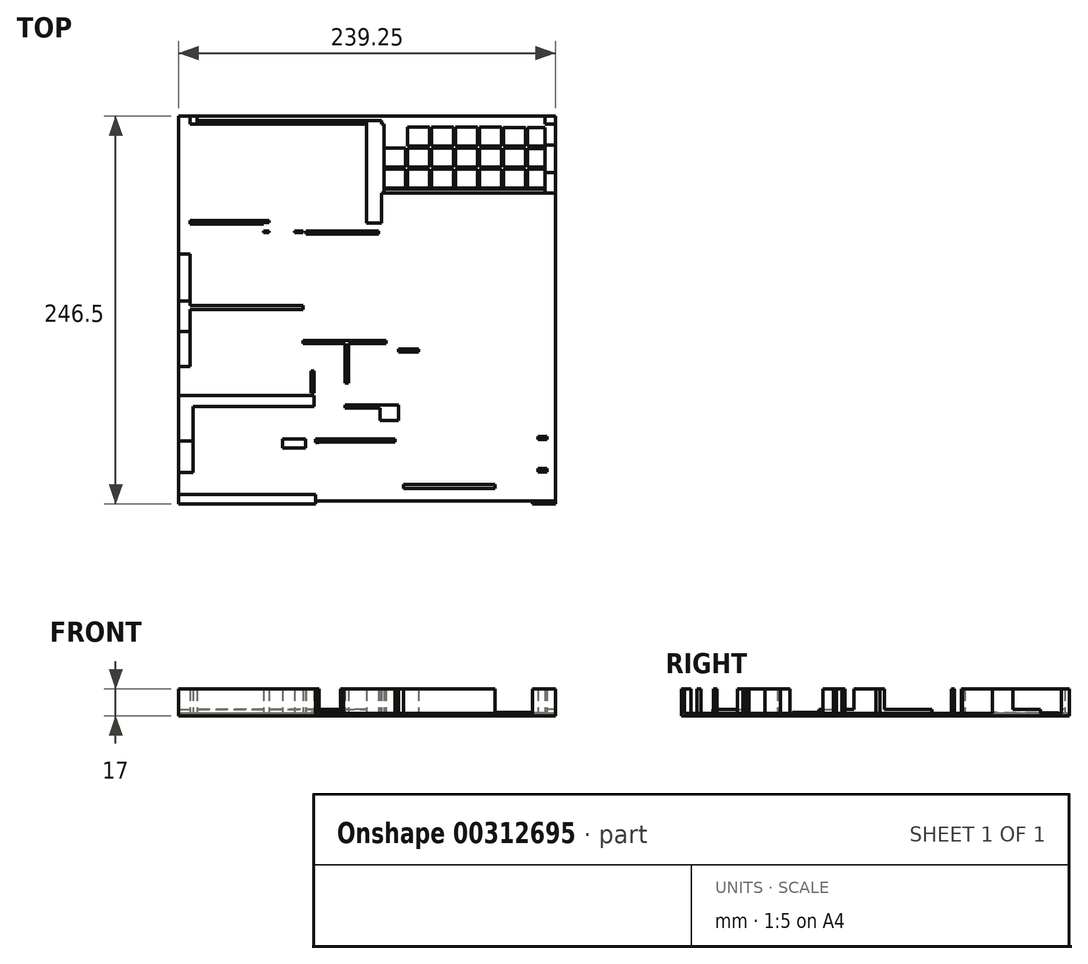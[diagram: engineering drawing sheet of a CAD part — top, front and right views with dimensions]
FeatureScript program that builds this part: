
annotation { "Feature Type Name" : "Feature", "Feature Type Description" : "" }
export const myFeature = defineFeature(function(context is Context, id is Id, definition is map)
    precondition{}
    {
        {
            var Q0;
            Q0=qCreatedBy(makeId("Top.planeOp"),FACE);
            var sketch = newSketch(context, id + "F0", { "sketchPlane" : qUnion([Q0])});
            skLineSegment(sketch, "E0.bottom", {"start": v(-71.69, -52.86) * mm, "end": v(15.31, -52.86) * mm});
            skLineSegment(sketch, "E0.top", {"start": v(-71.69, -46.86) * mm, "end": v(15.31, -46.86) * mm});
            skLineSegment(sketch, "E0.left", {"start": v(-71.69, -52.86) * mm, "end": v(-71.69, -46.86) * mm});
            skLineSegment(sketch, "E0.right", {"start": v(15.31, -52.86) * mm, "end": v(15.31, -46.86) * mm});
            skLineSegment(sketch, "E1.bottom", {"start": v(-71.69, -46.86) * mm, "end": v(-62.69, -46.86) * mm});
            skLineSegment(sketch, "E1.top", {"start": v(-71.69, -32.86) * mm, "end": v(-62.69, -32.86) * mm});
            skLineSegment(sketch, "E1.left", {"start": v(-71.69, -46.86) * mm, "end": v(-71.69, -32.86) * mm});
            skLineSegment(sketch, "E1.right", {"start": v(-62.69, -46.86) * mm, "end": v(-62.69, -32.86) * mm});
            skLineSegment(sketch, "E2.top", {"start": v(-71.69, -12.86) * mm, "end": v(-62.69, -12.86) * mm});
            skLineSegment(sketch, "E2.left", {"start": v(-71.69, -32.86) * mm, "end": v(-71.69, -12.86) * mm});
            skLineSegment(sketch, "E2.right", {"start": v(-62.69, -32.86) * mm, "end": v(-62.69, -12.86) * mm});
            skLineSegment(sketch, "E3.top", {"start": v(-71.69, 16.14) * mm, "end": v(-62.69, 16.14) * mm});
            skLineSegment(sketch, "E3.left", {"start": v(-71.69, -12.86) * mm, "end": v(-71.69, 16.14) * mm});
            skLineSegment(sketch, "E3.right", {"start": v(-62.69, -12.86) * mm, "end": v(-62.69, 16.14) * mm});
            skLineSegment(sketch, "E4.bottom", {"start": v(-71.69, 16.14) * mm, "end": v(-64.44, 16.14) * mm});
            skLineSegment(sketch, "E4.top", {"start": v(-71.69, 34.64) * mm, "end": v(-64.44, 34.64) * mm});
            skLineSegment(sketch, "E4.left", {"start": v(-71.69, 16.14) * mm, "end": v(-71.69, 34.64) * mm});
            skLineSegment(sketch, "E4.right", {"start": v(-64.44, 16.14) * mm, "end": v(-64.44, 34.64) * mm});
            skLineSegment(sketch, "E5.top", {"start": v(-71.69, 56.64) * mm, "end": v(-64.44, 56.64) * mm});
            skLineSegment(sketch, "E5.left", {"start": v(-71.69, 34.64) * mm, "end": v(-71.69, 56.64) * mm});
            skLineSegment(sketch, "E5.right", {"start": v(-64.44, 34.64) * mm, "end": v(-64.44, 56.64) * mm});
            skLineSegment(sketch, "E6.top", {"start": v(-71.69, 76.14) * mm, "end": v(-64.44, 76.14) * mm});
            skLineSegment(sketch, "E6.left", {"start": v(-71.69, 56.64) * mm, "end": v(-71.69, 76.14) * mm});
            skLineSegment(sketch, "E6.right", {"start": v(-64.44, 56.64) * mm, "end": v(-64.44, 76.14) * mm});
            skLineSegment(sketch, "E7.bottom", {"start": v(-62.69, 16.14) * mm, "end": v(14.31, 16.14) * mm});
            skLineSegment(sketch, "E7.top", {"start": v(-62.69, 9.14) * mm, "end": v(14.31, 9.14) * mm});
            skLineSegment(sketch, "E7.left", {"start": v(-62.69, 16.14) * mm, "end": v(-62.69, 9.14) * mm});
            skLineSegment(sketch, "E7.right", {"start": v(14.31, 16.14) * mm, "end": v(14.31, 9.14) * mm});
            skLineSegment(sketch, "E8.bottom", {"start": v(15.31, -46.86) * mm, "end": v(8.81, -46.86) * mm});
            skLineSegment(sketch, "E8.top", {"start": v(15.31, -11.36) * mm, "end": v(8.81, -11.36) * mm});
            skLineSegment(sketch, "E8.left", {"start": v(15.31, -46.86) * mm, "end": v(15.31, -11.36) * mm});
            skLineSegment(sketch, "E8.right", {"start": v(8.81, -46.86) * mm, "end": v(8.81, -11.36) * mm});
            skLineSegment(sketch, "E9.bottom", {"start": v(8.81, -11.36) * mm, "end": v(-5.69, -11.36) * mm});
            skLineSegment(sketch, "E9.top", {"start": v(8.81, -17.36) * mm, "end": v(-5.69, -17.36) * mm});
            skLineSegment(sketch, "E9.left", {"start": v(8.81, -11.36) * mm, "end": v(8.81, -17.36) * mm});
            skLineSegment(sketch, "E9.right", {"start": v(-5.69, -11.36) * mm, "end": v(-5.69, -17.36) * mm});
            skLineSegment(sketch, "E10.bottom", {"start": v(-5.69, -11.36) * mm, "end": v(-0.19, -11.36) * mm});
            skLineSegment(sketch, "E10.top", {"start": v(-5.69, -6.36) * mm, "end": v(-0.19, -6.36) * mm});
            skLineSegment(sketch, "E10.left", {"start": v(-5.69, -11.36) * mm, "end": v(-5.69, -6.36) * mm});
            skLineSegment(sketch, "E10.right", {"start": v(-0.19, -11.36) * mm, "end": v(-0.19, -6.36) * mm});
            skLineSegment(sketch, "E11", {"start": v(14.31, 9.14) * mm, "end": v(-0.19, 9.14) * mm, "construction": true});
            skLineSegment(sketch, "E12.bottom", {"start": v(-0.19, 9.14) * mm, "end": v(-5.19, 9.14) * mm});
            skLineSegment(sketch, "E12.top", {"start": v(-0.19, 7.64) * mm, "end": v(-5.19, 7.64) * mm});
            skLineSegment(sketch, "E12.left", {"start": v(-0.19, 9.14) * mm, "end": v(-0.19, 7.64) * mm});
            skLineSegment(sketch, "E12.right", {"start": v(-5.19, 9.14) * mm, "end": v(-5.19, 7.64) * mm});
            skLineSegment(sketch, "E13.bottom", {"start": v(15.31, -11.36) * mm, "end": v(17.31, -11.36) * mm});
            skLineSegment(sketch, "E13.top", {"start": v(15.31, -13.86) * mm, "end": v(17.31, -13.86) * mm});
            skLineSegment(sketch, "E13.left", {"start": v(15.31, -11.36) * mm, "end": v(15.31, -13.86) * mm});
            skLineSegment(sketch, "E13.right", {"start": v(17.31, -11.36) * mm, "end": v(17.31, -13.86) * mm});
            skLineSegment(sketch, "E14", {"start": v(-64.44, 76.14) * mm, "end": v(-64.44, 73.14) * mm, "construction": true});
            skLineSegment(sketch, "E15.bottom", {"start": v(-64.44, 73.14) * mm, "end": v(7.31, 73.14) * mm});
            skLineSegment(sketch, "E15.top", {"start": v(-64.44, 70.64) * mm, "end": v(7.31, 70.64) * mm});
            skLineSegment(sketch, "E15.left", {"start": v(-64.44, 73.14) * mm, "end": v(-64.44, 70.64) * mm});
            skLineSegment(sketch, "E15.right", {"start": v(7.31, 73.14) * mm, "end": v(7.31, 70.64) * mm});
            skLineSegment(sketch, "E16.bottom", {"start": v(14.31, 16.14) * mm, "end": v(12.31, 16.14) * mm});
            skLineSegment(sketch, "E16.top", {"start": v(14.31, 17.64) * mm, "end": v(12.31, 17.64) * mm});
            skLineSegment(sketch, "E16.left", {"start": v(14.31, 16.14) * mm, "end": v(14.31, 17.64) * mm});
            skLineSegment(sketch, "E16.right", {"start": v(12.31, 16.14) * mm, "end": v(12.31, 17.64) * mm});
            skLineSegment(sketch, "E17.top", {"start": v(14.31, 31.64) * mm, "end": v(12.31, 31.64) * mm});
            skLineSegment(sketch, "E17.left", {"start": v(14.31, 17.64) * mm, "end": v(14.31, 31.64) * mm});
            skLineSegment(sketch, "E17.right", {"start": v(12.31, 17.64) * mm, "end": v(12.31, 31.64) * mm});
            skLineSegment(sketch, "E18.bottom", {"start": v(12.31, 31.64) * mm, "end": v(14.31, 31.64) * mm});
            skLineSegment(sketch, "E18.top", {"start": v(12.31, 49.14) * mm, "end": v(14.31, 49.14) * mm});
            skLineSegment(sketch, "E18.left", {"start": v(12.31, 31.64) * mm, "end": v(12.31, 49.14) * mm});
            skLineSegment(sketch, "E18.right", {"start": v(14.31, 31.64) * mm, "end": v(14.31, 49.14) * mm});
            skLineSegment(sketch, "E19.bottom", {"start": v(12.31, 49.14) * mm, "end": v(7.31, 49.14) * mm});
            skLineSegment(sketch, "E19.top", {"start": v(12.31, 51.14) * mm, "end": v(7.31, 51.14) * mm});
            skLineSegment(sketch, "E19.left", {"start": v(12.31, 49.14) * mm, "end": v(12.31, 51.14) * mm});
            skLineSegment(sketch, "E19.right", {"start": v(7.31, 49.14) * mm, "end": v(7.31, 51.14) * mm});
            skLineSegment(sketch, "E20.bottom", {"start": v(12.31, 51.14) * mm, "end": v(17.31, 51.14) * mm});
            skLineSegment(sketch, "E20.top", {"start": v(12.31, 49.14) * mm, "end": v(17.31, 49.14) * mm});
            skLineSegment(sketch, "E20.left", {"start": v(12.31, 51.14) * mm, "end": v(12.31, 49.14) * mm});
            skLineSegment(sketch, "E20.right", {"start": v(17.31, 51.14) * mm, "end": v(17.31, 49.14) * mm});
            skLineSegment(sketch, "E21.bottom", {"start": v(7.31, 51.14) * mm, "end": v(9.31, 51.14) * mm});
            skLineSegment(sketch, "E21.top", {"start": v(7.31, 120.64) * mm, "end": v(9.31, 120.64) * mm});
            skLineSegment(sketch, "E21.left", {"start": v(7.31, 51.14) * mm, "end": v(7.31, 120.64) * mm});
            skLineSegment(sketch, "E21.right", {"start": v(9.31, 51.14) * mm, "end": v(9.31, 120.64) * mm});
            skLineSegment(sketch, "E22.top", {"start": v(-71.69, 106.14) * mm, "end": v(-64.44, 106.14) * mm});
            skLineSegment(sketch, "E22.left", {"start": v(-71.69, 76.14) * mm, "end": v(-71.69, 106.14) * mm});
            skLineSegment(sketch, "E22.right", {"start": v(-64.44, 76.14) * mm, "end": v(-64.44, 106.14) * mm});
            skLineSegment(sketch, "E23.bottom", {"start": v(-64.44, 106.14) * mm, "end": v(-71.69, 106.14) * mm});
            skLineSegment(sketch, "E23.top", {"start": v(-64.44, 193.64) * mm, "end": v(-71.69, 193.64) * mm});
            skLineSegment(sketch, "E23.left", {"start": v(-64.44, 106.14) * mm, "end": v(-64.44, 193.64) * mm});
            skLineSegment(sketch, "E23.right", {"start": v(-71.69, 106.14) * mm, "end": v(-71.69, 193.64) * mm});
            skLineSegment(sketch, "E24.bottom", {"start": v(9.31, 120.64) * mm, "end": v(16.81, 120.64) * mm});
            skLineSegment(sketch, "E24.top", {"start": v(9.31, 118.64) * mm, "end": v(16.81, 118.64) * mm});
            skLineSegment(sketch, "E24.left", {"start": v(9.31, 120.64) * mm, "end": v(9.31, 118.64) * mm});
            skLineSegment(sketch, "E24.right", {"start": v(16.81, 120.64) * mm, "end": v(16.81, 118.64) * mm});
            skLineSegment(sketch, "E25", {"start": v(-64.44, 106.14) * mm, "end": v(-64.44, 125.14) * mm, "construction": true});
            skLineSegment(sketch, "E26.bottom", {"start": v(-64.44, 125.14) * mm, "end": v(-17.94, 125.14) * mm});
            skLineSegment(sketch, "E26.top", {"start": v(-64.44, 127.14) * mm, "end": v(-17.94, 127.14) * mm});
            skLineSegment(sketch, "E26.left", {"start": v(-64.44, 125.14) * mm, "end": v(-64.44, 127.14) * mm});
            skLineSegment(sketch, "E26.right", {"start": v(-17.94, 125.14) * mm, "end": v(-17.94, 127.14) * mm});
            skLineSegment(sketch, "E27", {"start": v(-64.44, 127.14) * mm, "end": v(-58.44, 127.14) * mm, "construction": true});
            skLineSegment(sketch, "E28.bottom", {"start": v(-58.44, 127.14) * mm, "end": v(-56.44, 127.14) * mm});
            skLineSegment(sketch, "E28.top", {"start": v(-58.44, 136.64) * mm, "end": v(-56.44, 136.64) * mm});
            skLineSegment(sketch, "E28.left", {"start": v(-58.44, 127.14) * mm, "end": v(-58.44, 136.64) * mm});
            skLineSegment(sketch, "E28.right", {"start": v(-56.44, 127.14) * mm, "end": v(-56.44, 136.64) * mm});
            skLineSegment(sketch, "E29.bottom", {"start": v(-56.44, 136.64) * mm, "end": v(-64.44, 136.64) * mm});
            skLineSegment(sketch, "E29.top", {"start": v(-56.44, 134.14) * mm, "end": v(-64.44, 134.14) * mm});
            skLineSegment(sketch, "E29.left", {"start": v(-56.44, 136.64) * mm, "end": v(-56.44, 134.14) * mm});
            skLineSegment(sketch, "E29.right", {"start": v(-64.44, 136.64) * mm, "end": v(-64.44, 134.14) * mm});
            skLineSegment(sketch, "E30", {"start": v(-17.94, 127.14) * mm, "end": v(-29.94, 127.14) * mm, "construction": true});
            skLineSegment(sketch, "E31.bottom", {"start": v(-29.94, 127.14) * mm, "end": v(-31.94, 127.14) * mm});
            skLineSegment(sketch, "E31.top", {"start": v(-29.94, 149.14) * mm, "end": v(-31.94, 149.14) * mm});
            skLineSegment(sketch, "E31.left", {"start": v(-29.94, 127.14) * mm, "end": v(-29.94, 149.14) * mm});
            skLineSegment(sketch, "E31.right", {"start": v(-31.94, 127.14) * mm, "end": v(-31.94, 149.14) * mm});
            skLineSegment(sketch, "E32.bottom", {"start": v(-31.94, 149.14) * mm, "end": v(-29.94, 149.14) * mm});
            skLineSegment(sketch, "E32.top", {"start": v(-31.94, 163.14) * mm, "end": v(-29.94, 163.14) * mm});
            skLineSegment(sketch, "E32.left", {"start": v(-31.94, 149.14) * mm, "end": v(-31.94, 163.14) * mm});
            skLineSegment(sketch, "E32.right", {"start": v(-29.94, 149.14) * mm, "end": v(-29.94, 163.14) * mm});
            skLineSegment(sketch, "E33.bottom", {"start": v(-64.44, 193.64) * mm, "end": v(-59.94, 193.64) * mm});
            skLineSegment(sketch, "E33.top", {"start": v(-64.44, 188.64) * mm, "end": v(-59.94, 188.64) * mm});
            skLineSegment(sketch, "E33.left", {"start": v(-64.44, 193.64) * mm, "end": v(-64.44, 188.64) * mm});
            skLineSegment(sketch, "E33.right", {"start": v(-59.94, 193.64) * mm, "end": v(-59.94, 188.64) * mm});
            skLineSegment(sketch, "E34.bottom", {"start": v(-29.94, 163.14) * mm, "end": v(-31.94, 163.14) * mm});
            skLineSegment(sketch, "E34.top", {"start": v(-29.94, 188.64) * mm, "end": v(-31.94, 188.64) * mm});
            skLineSegment(sketch, "E34.left", {"start": v(-29.94, 163.14) * mm, "end": v(-29.94, 188.64) * mm});
            skLineSegment(sketch, "E34.right", {"start": v(-31.94, 163.14) * mm, "end": v(-31.94, 188.64) * mm});
            skLineSegment(sketch, "E35.bottom", {"start": v(-59.94, 188.64) * mm, "end": v(47.56, 188.64) * mm});
            skLineSegment(sketch, "E35.top", {"start": v(-59.94, 190.64) * mm, "end": v(47.56, 190.64) * mm});
            skLineSegment(sketch, "E35.left", {"start": v(-59.94, 188.64) * mm, "end": v(-59.94, 190.64) * mm});
            skLineSegment(sketch, "E35.right", {"start": v(47.56, 188.64) * mm, "end": v(47.56, 190.64) * mm});
            skLineSegment(sketch, "E36.bottom", {"start": v(47.56, 190.64) * mm, "end": v(57.06, 190.64) * mm});
            skLineSegment(sketch, "E36.top", {"start": v(47.56, 125.64) * mm, "end": v(57.06, 125.64) * mm});
            skLineSegment(sketch, "E36.left", {"start": v(47.56, 190.64) * mm, "end": v(47.56, 125.64) * mm});
            skLineSegment(sketch, "E36.right", {"start": v(57.06, 190.64) * mm, "end": v(57.06, 125.64) * mm});
            skLineSegment(sketch, "E37.bottom", {"start": v(47.56, 125.64) * mm, "end": v(49.56, 125.64) * mm});
            skLineSegment(sketch, "E38.bottom", {"start": v(55.06, 118.64) * mm, "end": v(31.06, 118.64) * mm});
            skLineSegment(sketch, "E38.top", {"start": v(55.06, 120.64) * mm, "end": v(31.06, 120.64) * mm});
            skLineSegment(sketch, "E38.left", {"start": v(55.06, 118.64) * mm, "end": v(55.06, 120.64) * mm});
            skLineSegment(sketch, "E38.right", {"start": v(31.06, 118.64) * mm, "end": v(31.06, 120.64) * mm});
            skLineSegment(sketch, "E39", {"start": v(57.06, 190.64) * mm, "end": v(57.06, 188.64) * mm, "construction": true});
            skLineSegment(sketch, "E40.bottom", {"start": v(57.06, 188.64) * mm, "end": v(58.56, 188.64) * mm});
            skLineSegment(sketch, "E40.top", {"start": v(57.06, 144.64) * mm, "end": v(58.56, 144.64) * mm});
            skLineSegment(sketch, "E40.left", {"start": v(57.06, 188.64) * mm, "end": v(57.06, 144.64) * mm, "construction": true});
            skLineSegment(sketch, "E40.right", {"start": v(58.56, 188.64) * mm, "end": v(58.56, 144.64) * mm});
            skLineSegment(sketch, "E41.bottom", {"start": v(58.56, 188.64) * mm, "end": v(161.06, 188.64) * mm});
            skLineSegment(sketch, "E41.top", {"start": v(58.56, 186.64) * mm, "end": v(161.06, 186.64) * mm});
            skLineSegment(sketch, "E41.left", {"start": v(58.56, 188.64) * mm, "end": v(58.56, 186.64) * mm});
            skLineSegment(sketch, "E41.right", {"start": v(161.06, 188.64) * mm, "end": v(161.06, 186.64) * mm});
            skLineSegment(sketch, "E42.bottom", {"start": v(161.06, 188.64) * mm, "end": v(167.56, 188.64) * mm});
            skLineSegment(sketch, "E42.top", {"start": v(161.06, 193.64) * mm, "end": v(167.56, 193.64) * mm});
            skLineSegment(sketch, "E42.left", {"start": v(161.06, 188.64) * mm, "end": v(161.06, 193.64) * mm});
            skLineSegment(sketch, "E42.right", {"start": v(167.56, 188.64) * mm, "end": v(167.56, 193.64) * mm});
            skLineSegment(sketch, "E43.bottom", {"start": v(167.56, 188.64) * mm, "end": v(161.06, 188.64) * mm});
            skLineSegment(sketch, "E43.top", {"start": v(167.56, 175.14) * mm, "end": v(161.06, 175.14) * mm});
            skLineSegment(sketch, "E43.left", {"start": v(167.56, 188.64) * mm, "end": v(167.56, 175.14) * mm});
            skLineSegment(sketch, "E43.right", {"start": v(161.06, 188.64) * mm, "end": v(161.06, 175.14) * mm});
            skLineSegment(sketch, "E44.top", {"start": v(167.56, 157.64) * mm, "end": v(161.06, 157.64) * mm});
            skLineSegment(sketch, "E44.left", {"start": v(167.56, 175.14) * mm, "end": v(167.56, 157.64) * mm});
            skLineSegment(sketch, "E44.right", {"start": v(161.06, 175.14) * mm, "end": v(161.06, 157.64) * mm});
            skLineSegment(sketch, "E45.top", {"start": v(167.56, 144.64) * mm, "end": v(161.06, 144.64) * mm});
            skLineSegment(sketch, "E45.left", {"start": v(167.56, 157.64) * mm, "end": v(167.56, 144.64) * mm});
            skLineSegment(sketch, "E45.right", {"start": v(161.06, 157.64) * mm, "end": v(161.06, 144.64) * mm});
            skLineSegment(sketch, "E46.bottom", {"start": v(167.56, 144.64) * mm, "end": v(162.06, 144.64) * mm});
            skLineSegment(sketch, "E46.top", {"start": v(167.56, -50.86) * mm, "end": v(162.06, -50.86) * mm});
            skLineSegment(sketch, "E46.left", {"start": v(167.56, 144.64) * mm, "end": v(167.56, -50.86) * mm});
            skLineSegment(sketch, "E46.right", {"start": v(162.06, 144.64) * mm, "end": v(162.06, -50.86) * mm});
            skLineSegment(sketch, "E47.bottom", {"start": v(15.31, -52.86) * mm, "end": v(167.56, -52.86) * mm});
            skLineSegment(sketch, "E47.top", {"start": v(15.31, -50.86) * mm, "end": v(167.56, -50.86) * mm});
            skLineSegment(sketch, "E47.left", {"start": v(15.31, -52.86) * mm, "end": v(15.31, -50.86) * mm});
            skLineSegment(sketch, "E47.right", {"start": v(167.56, -52.86) * mm, "end": v(167.56, -50.86) * mm});
            skLineSegment(sketch, "E48", {"start": v(162.06, -50.86) * mm, "end": v(153.06, -50.86) * mm, "construction": true});
            skLineSegment(sketch, "E49.bottom", {"start": v(153.06, -50.86) * mm, "end": v(133.06, -50.86) * mm});
            skLineSegment(sketch, "E49.top", {"start": v(153.06, -52.86) * mm, "end": v(133.06, -52.86) * mm});
            skLineSegment(sketch, "E49.left", {"start": v(153.06, -50.86) * mm, "end": v(153.06, -52.86) * mm});
            skLineSegment(sketch, "E49.right", {"start": v(133.06, -50.86) * mm, "end": v(133.06, -52.86) * mm});
            skLineSegment(sketch, "E50", {"start": v(133.06, -50.86) * mm, "end": v(131.06, -50.86) * mm, "construction": true});
            skLineSegment(sketch, "E51.bottom", {"start": v(131.06, -50.86) * mm, "end": v(129.06, -50.86) * mm});
            skLineSegment(sketch, "E51.top", {"start": v(131.06, -30.86) * mm, "end": v(129.06, -30.86) * mm});
            skLineSegment(sketch, "E51.left", {"start": v(131.06, -50.86) * mm, "end": v(131.06, -30.86) * mm});
            skLineSegment(sketch, "E51.right", {"start": v(129.06, -50.86) * mm, "end": v(129.06, -30.86) * mm});
            skLineSegment(sketch, "E52.bottom", {"start": v(129.06, -50.86) * mm, "end": v(103.06, -50.86) * mm});
            skLineSegment(sketch, "E52.top", {"start": v(129.06, -42.86) * mm, "end": v(103.06, -42.86) * mm});
            skLineSegment(sketch, "E52.left", {"start": v(129.06, -50.86) * mm, "end": v(129.06, -42.86) * mm});
            skLineSegment(sketch, "E52.right", {"start": v(103.06, -50.86) * mm, "end": v(103.06, -42.86) * mm});
            skLineSegment(sketch, "E53.bottom", {"start": v(103.06, -42.86) * mm, "end": v(101.06, -42.86) * mm});
            skLineSegment(sketch, "E53.top", {"start": v(103.06, -50.86) * mm, "end": v(101.06, -50.86) * mm});
            skLineSegment(sketch, "E53.left", {"start": v(103.06, -42.86) * mm, "end": v(103.06, -50.86) * mm});
            skLineSegment(sketch, "E53.right", {"start": v(101.06, -42.86) * mm, "end": v(101.06, -50.86) * mm});
            skLineSegment(sketch, "E54.bottom", {"start": v(101.06, -42.86) * mm, "end": v(71.06, -42.86) * mm});
            skLineSegment(sketch, "E54.top", {"start": v(101.06, -50.86) * mm, "end": v(71.06, -50.86) * mm});
            skLineSegment(sketch, "E54.right", {"start": v(71.06, -42.86) * mm, "end": v(71.06, -50.86) * mm});
            skLineSegment(sketch, "E55.bottom", {"start": v(71.06, -50.86) * mm, "end": v(65.56, -50.86) * mm});
            skLineSegment(sketch, "E55.top", {"start": v(71.06, -40.36) * mm, "end": v(65.56, -40.36) * mm});
            skLineSegment(sketch, "E55.left", {"start": v(71.06, -50.86) * mm, "end": v(71.06, -40.36) * mm});
            skLineSegment(sketch, "E55.right", {"start": v(65.56, -50.86) * mm, "end": v(65.56, -40.36) * mm});
            skLineSegment(sketch, "E56.bottom", {"start": v(71.06, -40.36) * mm, "end": v(129.06, -40.36) * mm});
            skLineSegment(sketch, "E56.top", {"start": v(71.06, -42.86) * mm, "end": v(129.06, -42.86) * mm});
            skLineSegment(sketch, "E56.left", {"start": v(71.06, -40.36) * mm, "end": v(71.06, -42.86) * mm});
            skLineSegment(sketch, "E56.right", {"start": v(129.06, -40.36) * mm, "end": v(129.06, -42.86) * mm});
            skLineSegment(sketch, "E57.bottom", {"start": v(65.56, -40.36) * mm, "end": v(68.06, -40.36) * mm});
            skLineSegment(sketch, "E57.top", {"start": v(65.56, 0.14) * mm, "end": v(68.06, 0.14) * mm});
            skLineSegment(sketch, "E57.left", {"start": v(65.56, -40.36) * mm, "end": v(65.56, 0.14) * mm});
            skLineSegment(sketch, "E57.right", {"start": v(68.06, -40.36) * mm, "end": v(68.06, 0.14) * mm});
            skLineSegment(sketch, "E58.bottom", {"start": v(68.06, 0.14) * mm, "end": v(56.06, 0.14) * mm});
            skLineSegment(sketch, "E58.top", {"start": v(68.06, 10.14) * mm, "end": v(56.06, 10.14) * mm});
            skLineSegment(sketch, "E58.left", {"start": v(68.06, 0.14) * mm, "end": v(68.06, 10.14) * mm});
            skLineSegment(sketch, "E58.right", {"start": v(56.06, 0.14) * mm, "end": v(56.06, 10.14) * mm});
            skLineSegment(sketch, "E59.bottom", {"start": v(68.06, 10.14) * mm, "end": v(60.06, 10.14) * mm});
            skLineSegment(sketch, "E59.top", {"start": v(68.06, 51.14) * mm, "end": v(60.06, 51.14) * mm});
            skLineSegment(sketch, "E59.left", {"start": v(68.06, 10.14) * mm, "end": v(68.06, 51.14) * mm});
            skLineSegment(sketch, "E59.right", {"start": v(60.06, 10.14) * mm, "end": v(60.06, 51.14) * mm});
            skLineSegment(sketch, "E60.bottom", {"start": v(60.06, 51.14) * mm, "end": v(32.56, 51.14) * mm});
            skLineSegment(sketch, "E60.top", {"start": v(60.06, 49.14) * mm, "end": v(32.56, 49.14) * mm});
            skLineSegment(sketch, "E60.left", {"start": v(60.06, 51.14) * mm, "end": v(60.06, 49.14) * mm});
            skLineSegment(sketch, "E60.right", {"start": v(32.56, 51.14) * mm, "end": v(32.56, 49.14) * mm});
            skLineSegment(sketch, "E61.bottom", {"start": v(32.56, 51.14) * mm, "end": v(17.31, 51.14) * mm});
            skLineSegment(sketch, "E61.top", {"start": v(32.56, 49.14) * mm, "end": v(17.31, 49.14) * mm});
            skLineSegment(sketch, "E62.bottom", {"start": v(56.06, 0.14) * mm, "end": v(58.06, 0.14) * mm});
            skLineSegment(sketch, "E62.top", {"start": v(56.06, -11.36) * mm, "end": v(58.06, -11.36) * mm});
            skLineSegment(sketch, "E62.left", {"start": v(56.06, 0.14) * mm, "end": v(56.06, -11.36) * mm});
            skLineSegment(sketch, "E62.right", {"start": v(58.06, 0.14) * mm, "end": v(58.06, -11.36) * mm});
            skLineSegment(sketch, "E63.bottom", {"start": v(58.06, -11.36) * mm, "end": v(65.56, -11.36) * mm});
            skLineSegment(sketch, "E63.top", {"start": v(58.06, -13.36) * mm, "end": v(65.56, -13.36) * mm});
            skLineSegment(sketch, "E63.left", {"start": v(58.06, -11.36) * mm, "end": v(58.06, -13.36) * mm});
            skLineSegment(sketch, "E63.right", {"start": v(65.56, -11.36) * mm, "end": v(65.56, -13.36) * mm});
            skLineSegment(sketch, "E64.bottom", {"start": v(58.06, -11.36) * mm, "end": v(33.06, -11.36) * mm});
            skLineSegment(sketch, "E64.top", {"start": v(58.06, -13.36) * mm, "end": v(33.06, -13.36) * mm});
            skLineSegment(sketch, "E64.right", {"start": v(33.06, -11.36) * mm, "end": v(33.06, -13.36) * mm});
            skLineSegment(sketch, "E65.bottom", {"start": v(17.31, -11.36) * mm, "end": v(33.06, -11.36) * mm});
            skLineSegment(sketch, "E65.top", {"start": v(17.31, -13.36) * mm, "end": v(33.06, -13.36) * mm});
            skLineSegment(sketch, "E65.left", {"start": v(17.31, -11.36) * mm, "end": v(17.31, -13.36) * mm});
            skLineSegment(sketch, "E66.bottom", {"start": v(56.06, 10.14) * mm, "end": v(34.06, 10.14) * mm});
            skLineSegment(sketch, "E66.top", {"start": v(56.06, 8.14) * mm, "end": v(34.06, 8.14) * mm});
            skLineSegment(sketch, "E66.left", {"start": v(56.06, 10.14) * mm, "end": v(56.06, 8.14) * mm});
            skLineSegment(sketch, "E66.right", {"start": v(34.06, 10.14) * mm, "end": v(34.06, 8.14) * mm});
            skLineSegment(sketch, "E67.bottom", {"start": v(34.06, 10.14) * mm, "end": v(36.06, 10.14) * mm});
            skLineSegment(sketch, "E67.top", {"start": v(34.06, 24.14) * mm, "end": v(36.06, 24.14) * mm});
            skLineSegment(sketch, "E67.left", {"start": v(34.06, 10.14) * mm, "end": v(34.06, 24.14) * mm});
            skLineSegment(sketch, "E67.right", {"start": v(36.06, 10.14) * mm, "end": v(36.06, 24.14) * mm});
            skLineSegment(sketch, "E68.top", {"start": v(34.06, 37.14) * mm, "end": v(36.06, 37.14) * mm});
            skLineSegment(sketch, "E68.left", {"start": v(34.06, 24.14) * mm, "end": v(34.06, 37.14) * mm});
            skLineSegment(sketch, "E68.right", {"start": v(36.06, 24.14) * mm, "end": v(36.06, 37.14) * mm});
            skLineSegment(sketch, "E69.top", {"start": v(34.06, 49.14) * mm, "end": v(36.06, 49.14) * mm});
            skLineSegment(sketch, "E69.left", {"start": v(34.06, 37.14) * mm, "end": v(34.06, 49.14) * mm});
            skLineSegment(sketch, "E69.right", {"start": v(36.06, 37.14) * mm, "end": v(36.06, 49.14) * mm});
            skLineSegment(sketch, "E70", {"start": v(68.06, 51.14) * mm, "end": v(68.06, 45.64) * mm, "construction": true});
            skLineSegment(sketch, "E71.bottom", {"start": v(68.06, 45.64) * mm, "end": v(80.56, 45.64) * mm});
            skLineSegment(sketch, "E71.top", {"start": v(68.06, 43.64) * mm, "end": v(80.56, 43.64) * mm});
            skLineSegment(sketch, "E71.left", {"start": v(68.06, 45.64) * mm, "end": v(68.06, 43.64) * mm});
            skLineSegment(sketch, "E71.right", {"start": v(80.56, 45.64) * mm, "end": v(80.56, 43.64) * mm});
            skLineSegment(sketch, "E72", {"start": v(162.06, -50.86) * mm, "end": v(162.06, -32.36) * mm, "construction": true});
            skLineSegment(sketch, "E73.bottom", {"start": v(162.06, -32.36) * mm, "end": v(156.56, -32.36) * mm});
            skLineSegment(sketch, "E73.top", {"start": v(162.06, -30.36) * mm, "end": v(156.56, -30.36) * mm});
            skLineSegment(sketch, "E73.left", {"start": v(162.06, -32.36) * mm, "end": v(162.06, -30.36) * mm});
            skLineSegment(sketch, "E73.right", {"start": v(156.56, -32.36) * mm, "end": v(156.56, -30.36) * mm});
            skLineSegment(sketch, "E74", {"start": v(162.06, -30.36) * mm, "end": v(162.06, -11.86) * mm, "construction": true});
            skLineSegment(sketch, "E75.bottom", {"start": v(162.06, -11.86) * mm, "end": v(156.56, -11.86) * mm});
            skLineSegment(sketch, "E75.top", {"start": v(162.06, -9.86) * mm, "end": v(156.56, -9.86) * mm});
            skLineSegment(sketch, "E75.left", {"start": v(162.06, -11.86) * mm, "end": v(162.06, -9.86) * mm});
            skLineSegment(sketch, "E75.right", {"start": v(156.56, -11.86) * mm, "end": v(156.56, -9.86) * mm});
            skLineSegment(sketch, "E76.bottom", {"start": v(58.56, 144.64) * mm, "end": v(161.06, 144.64) * mm});
            skLineSegment(sketch, "E76.top", {"start": v(58.56, 147.14) * mm, "end": v(161.06, 147.14) * mm});
            skLineSegment(sketch, "E76.left", {"start": v(58.56, 144.64) * mm, "end": v(58.56, 147.14) * mm});
            skLineSegment(sketch, "E76.right", {"start": v(161.06, 144.64) * mm, "end": v(161.06, 147.14) * mm});
            skLineSegment(sketch, "E77.bottom", {"start": v(-71.69, 193.64) * mm, "end": v(167.56, 193.64) * mm});
            skLineSegment(sketch, "E77.top", {"start": v(-71.69, -52.86) * mm, "end": v(167.56, -52.86) * mm});
            skLineSegment(sketch, "E77.left", {"start": v(-71.69, 193.64) * mm, "end": v(-71.69, -52.86) * mm});
            skLineSegment(sketch, "E77.right", {"start": v(167.56, 193.64) * mm, "end": v(167.56, -52.86) * mm});
            skLineSegment(sketch, "E78.bottom", {"start": v(57.06, 125.64) * mm, "end": v(55.06, 125.64) * mm});
            skLineSegment(sketch, "E78.top", {"start": v(57.06, 118.64) * mm, "end": v(55.06, 118.64) * mm});
            skLineSegment(sketch, "E78.left", {"start": v(57.06, 125.64) * mm, "end": v(57.06, 118.64) * mm});
            skLineSegment(sketch, "E78.right", {"start": v(55.06, 125.64) * mm, "end": v(55.06, 118.64) * mm});
            skLineSegment(sketch, "E79.bottom", {"start": v(16.81, 120.64) * mm, "end": v(31.06, 120.64) * mm});
            skLineSegment(sketch, "E79.top", {"start": v(16.81, 118.64) * mm, "end": v(31.06, 118.64) * mm});
            skLineSegment(sketch, "E79.right", {"start": v(31.06, 120.64) * mm, "end": v(31.06, 118.64) * mm});
            skLineSegment(sketch, "E80.bottom", {"start": v(-17.94, 127.14) * mm, "end": v(-14.44, 127.14) * mm});
            skLineSegment(sketch, "E80.top", {"start": v(-17.94, 126.14) * mm, "end": v(-14.44, 126.14) * mm});
            skLineSegment(sketch, "E80.left", {"start": v(-17.94, 127.14) * mm, "end": v(-17.94, 126.14) * mm});
            skLineSegment(sketch, "E80.right", {"start": v(-14.44, 127.14) * mm, "end": v(-14.44, 126.14) * mm});
            skLineSegment(sketch, "E81.bottom", {"start": v(-17.94, 125.14) * mm, "end": v(-18.94, 125.14) * mm});
            skLineSegment(sketch, "E81.top", {"start": v(-17.94, 117.64) * mm, "end": v(-18.94, 117.64) * mm});
            skLineSegment(sketch, "E81.left", {"start": v(-17.94, 125.14) * mm, "end": v(-17.94, 117.64) * mm});
            skLineSegment(sketch, "E81.right", {"start": v(-18.94, 125.14) * mm, "end": v(-18.94, 117.64) * mm});
            skLineSegment(sketch, "E82.bottom", {"start": v(7.31, 120.64) * mm, "end": v(1.81, 120.64) * mm});
            skLineSegment(sketch, "E82.top", {"start": v(7.31, 119.64) * mm, "end": v(1.81, 119.64) * mm});
            skLineSegment(sketch, "E82.left", {"start": v(7.31, 120.64) * mm, "end": v(7.31, 119.64) * mm});
            skLineSegment(sketch, "E82.right", {"start": v(1.81, 120.64) * mm, "end": v(1.81, 119.64) * mm});
            skLineSegment(sketch, "E83.bottom", {"start": v(-17.94, 120.64) * mm, "end": v(-14.44, 120.64) * mm});
            skLineSegment(sketch, "E83.top", {"start": v(-17.94, 119.64) * mm, "end": v(-14.44, 119.64) * mm});
            skLineSegment(sketch, "E83.left", {"start": v(-17.94, 120.64) * mm, "end": v(-17.94, 119.64) * mm});
            skLineSegment(sketch, "E83.right", {"start": v(-14.44, 120.64) * mm, "end": v(-14.44, 119.64) * mm});
            skLineSegment(sketch, "E84.bottom", {"start": v(-5.19, 7.64) * mm, "end": v(-0.19, 7.64) * mm});
            skLineSegment(sketch, "E84.top", {"start": v(-5.19, -6.36) * mm, "end": v(-0.19, -6.36) * mm});
            skLineSegment(sketch, "E84.left", {"start": v(-5.19, 7.64) * mm, "end": v(-5.19, -6.36) * mm});
            skLineSegment(sketch, "E84.right", {"start": v(-0.19, 7.64) * mm, "end": v(-0.19, -6.36) * mm});
            skSolve(sketch);
        }
        {
            var Q0;
            Q0=makeQuery(id+"F0.imprint","IMPRINT",FACE,{"disambiguationData":[TD([[makeQuery(id+"F0.imprint","IMPRINT",EDGE,{"derivedFrom":sQuery(id+"F0.wireOp",EDGE,"E40.right")}),1.0]])]});
            var sketch = newSketch(context, id + "F1", { "sketchPlane" : qUnion([Q0])});
            skLineSegment(sketch, "E85.0", {"start": v(58.56, 188.64) * mm, "end": v(58.56, 144.64) * mm});
            skLineSegment(sketch, "E86.0", {"start": v(161.06, 188.64) * mm, "end": v(161.06, 175.14) * mm});
            skLineSegment(sketch, "E87.0", {"start": v(161.06, 175.14) * mm, "end": v(161.06, 157.64) * mm});
            skLineSegment(sketch, "E88.0", {"start": v(161.06, 157.64) * mm, "end": v(161.06, 144.64) * mm});
            skLineSegment(sketch, "E89.0", {"start": v(58.56, 147.14) * mm, "end": v(161.06, 147.14) * mm});
            skLineSegment(sketch, "E90.0", {"start": v(58.56, 186.64) * mm, "end": v(161.06, 186.64) * mm});
            skLineSegment(sketch, "E91.bottom", {"start": v(58.56, 186.64) * mm, "end": v(72.5, 186.64) * mm});
            skLineSegment(sketch, "E91.top", {"start": v(58.56, 174.62) * mm, "end": v(72.5, 174.62) * mm});
            skLineSegment(sketch, "E91.left", {"start": v(58.56, 186.64) * mm, "end": v(58.56, 174.62) * mm});
            skLineSegment(sketch, "E91.right", {"start": v(72.5, 186.64) * mm, "end": v(72.5, 174.62) * mm});
            skLineSegment(sketch, "E92.0.1.0", {"start": v(58.56, 173.34) * mm, "end": v(72.5, 173.34) * mm});
            skLineSegment(sketch, "E92.0.1.1", {"start": v(72.5, 173.34) * mm, "end": v(72.5, 161.32) * mm});
            skLineSegment(sketch, "E92.0.1.2", {"start": v(58.56, 161.32) * mm, "end": v(72.5, 161.32) * mm});
            skLineSegment(sketch, "E92.0.1.3", {"start": v(58.56, 173.34) * mm, "end": v(58.56, 161.32) * mm});
            skLineSegment(sketch, "E92.0.2.0", {"start": v(58.56, 160.04) * mm, "end": v(72.5, 160.04) * mm});
            skLineSegment(sketch, "E92.0.2.1", {"start": v(72.5, 160.04) * mm, "end": v(72.5, 148.02) * mm});
            skLineSegment(sketch, "E92.0.2.2", {"start": v(58.56, 148.02) * mm, "end": v(72.5, 148.02) * mm});
            skLineSegment(sketch, "E92.0.2.3", {"start": v(58.56, 160.04) * mm, "end": v(58.56, 148.02) * mm});
            skLineSegment(sketch, "E92.1.0.0", {"start": v(73.76, 186.6) * mm, "end": v(87.7, 186.6) * mm});
            skLineSegment(sketch, "E92.1.0.1", {"start": v(87.7, 186.6) * mm, "end": v(87.7, 174.59) * mm});
            skLineSegment(sketch, "E92.1.0.2", {"start": v(73.76, 174.59) * mm, "end": v(87.7, 174.59) * mm});
            skLineSegment(sketch, "E92.1.0.3", {"start": v(73.76, 186.6) * mm, "end": v(73.76, 174.59) * mm});
            skLineSegment(sketch, "E92.1.1.0", {"start": v(73.76, 173.3) * mm, "end": v(87.7, 173.3) * mm});
            skLineSegment(sketch, "E92.1.1.1", {"start": v(87.7, 173.3) * mm, "end": v(87.7, 161.29) * mm});
            skLineSegment(sketch, "E92.1.1.2", {"start": v(73.76, 161.29) * mm, "end": v(87.7, 161.29) * mm});
            skLineSegment(sketch, "E92.1.1.3", {"start": v(73.76, 173.3) * mm, "end": v(73.76, 161.29) * mm});
            skLineSegment(sketch, "E92.1.2.0", {"start": v(73.76, 160) * mm, "end": v(87.7, 160) * mm});
            skLineSegment(sketch, "E92.1.2.1", {"start": v(87.7, 160) * mm, "end": v(87.7, 147.99) * mm});
            skLineSegment(sketch, "E92.1.2.2", {"start": v(73.76, 147.99) * mm, "end": v(87.7, 147.99) * mm});
            skLineSegment(sketch, "E92.1.2.3", {"start": v(73.76, 160) * mm, "end": v(73.76, 147.99) * mm});
            skLineSegment(sketch, "E92.2.0.0", {"start": v(88.96, 186.57) * mm, "end": v(102.9, 186.57) * mm});
            skLineSegment(sketch, "E92.2.0.1", {"start": v(102.9, 186.57) * mm, "end": v(102.9, 174.55) * mm});
            skLineSegment(sketch, "E92.2.0.2", {"start": v(88.96, 174.55) * mm, "end": v(102.9, 174.55) * mm});
            skLineSegment(sketch, "E92.2.0.3", {"start": v(88.96, 186.57) * mm, "end": v(88.96, 174.55) * mm});
            skLineSegment(sketch, "E92.2.1.0", {"start": v(88.96, 173.27) * mm, "end": v(102.9, 173.27) * mm});
            skLineSegment(sketch, "E92.2.1.1", {"start": v(102.9, 173.27) * mm, "end": v(102.9, 161.25) * mm});
            skLineSegment(sketch, "E92.2.1.2", {"start": v(88.96, 161.25) * mm, "end": v(102.9, 161.25) * mm});
            skLineSegment(sketch, "E92.2.1.3", {"start": v(88.96, 173.27) * mm, "end": v(88.96, 161.25) * mm});
            skLineSegment(sketch, "E92.2.2.0", {"start": v(88.96, 159.97) * mm, "end": v(102.9, 159.97) * mm});
            skLineSegment(sketch, "E92.2.2.1", {"start": v(102.9, 159.97) * mm, "end": v(102.9, 147.95) * mm});
            skLineSegment(sketch, "E92.2.2.2", {"start": v(88.96, 147.95) * mm, "end": v(102.9, 147.95) * mm});
            skLineSegment(sketch, "E92.2.2.3", {"start": v(88.96, 159.97) * mm, "end": v(88.96, 147.95) * mm});
            skLineSegment(sketch, "E92.3.0.0", {"start": v(104.16, 186.53) * mm, "end": v(118.1, 186.53) * mm});
            skLineSegment(sketch, "E92.3.0.1", {"start": v(118.1, 186.53) * mm, "end": v(118.1, 174.52) * mm});
            skLineSegment(sketch, "E92.3.0.2", {"start": v(104.16, 174.52) * mm, "end": v(118.1, 174.52) * mm});
            skLineSegment(sketch, "E92.3.0.3", {"start": v(104.16, 186.53) * mm, "end": v(104.16, 174.52) * mm});
            skLineSegment(sketch, "E92.3.1.0", {"start": v(104.16, 173.23) * mm, "end": v(118.1, 173.23) * mm});
            skLineSegment(sketch, "E92.3.1.1", {"start": v(118.1, 173.23) * mm, "end": v(118.1, 161.22) * mm});
            skLineSegment(sketch, "E92.3.1.2", {"start": v(104.16, 161.22) * mm, "end": v(118.1, 161.22) * mm});
            skLineSegment(sketch, "E92.3.1.3", {"start": v(104.16, 173.23) * mm, "end": v(104.16, 161.22) * mm});
            skLineSegment(sketch, "E92.3.2.0", {"start": v(104.16, 159.93) * mm, "end": v(118.1, 159.93) * mm});
            skLineSegment(sketch, "E92.3.2.1", {"start": v(118.1, 159.93) * mm, "end": v(118.1, 147.92) * mm});
            skLineSegment(sketch, "E92.3.2.2", {"start": v(104.16, 147.92) * mm, "end": v(118.1, 147.92) * mm});
            skLineSegment(sketch, "E92.3.2.3", {"start": v(104.16, 159.93) * mm, "end": v(104.16, 147.92) * mm});
            skLineSegment(sketch, "E92.4.0.0", {"start": v(119.36, 186.5) * mm, "end": v(133.3, 186.5) * mm});
            skLineSegment(sketch, "E92.4.0.1", {"start": v(133.3, 186.5) * mm, "end": v(133.3, 174.48) * mm});
            skLineSegment(sketch, "E92.4.0.2", {"start": v(119.36, 174.48) * mm, "end": v(133.3, 174.48) * mm});
            skLineSegment(sketch, "E92.4.0.3", {"start": v(119.36, 186.5) * mm, "end": v(119.36, 174.48) * mm});
            skLineSegment(sketch, "E92.4.1.0", {"start": v(119.36, 173.2) * mm, "end": v(133.3, 173.2) * mm});
            skLineSegment(sketch, "E92.4.1.1", {"start": v(133.3, 173.2) * mm, "end": v(133.3, 161.18) * mm});
            skLineSegment(sketch, "E92.4.1.2", {"start": v(119.36, 161.18) * mm, "end": v(133.3, 161.18) * mm});
            skLineSegment(sketch, "E92.4.1.3", {"start": v(119.36, 173.2) * mm, "end": v(119.36, 161.18) * mm});
            skLineSegment(sketch, "E92.4.2.0", {"start": v(119.36, 159.9) * mm, "end": v(133.3, 159.9) * mm});
            skLineSegment(sketch, "E92.4.2.1", {"start": v(133.3, 159.9) * mm, "end": v(133.3, 147.88) * mm});
            skLineSegment(sketch, "E92.4.2.2", {"start": v(119.36, 147.88) * mm, "end": v(133.3, 147.88) * mm});
            skLineSegment(sketch, "E92.4.2.3", {"start": v(119.36, 159.9) * mm, "end": v(119.36, 147.88) * mm});
            skLineSegment(sketch, "E92.5.0.0", {"start": v(134.56, 186.46) * mm, "end": v(148.5, 186.46) * mm});
            skLineSegment(sketch, "E92.5.0.1", {"start": v(148.5, 186.46) * mm, "end": v(148.5, 174.45) * mm});
            skLineSegment(sketch, "E92.5.0.2", {"start": v(134.56, 174.45) * mm, "end": v(148.5, 174.45) * mm});
            skLineSegment(sketch, "E92.5.0.3", {"start": v(134.56, 186.46) * mm, "end": v(134.56, 174.45) * mm});
            skLineSegment(sketch, "E92.5.1.0", {"start": v(134.56, 173.16) * mm, "end": v(148.5, 173.16) * mm});
            skLineSegment(sketch, "E92.5.1.1", {"start": v(148.5, 173.16) * mm, "end": v(148.5, 161.15) * mm});
            skLineSegment(sketch, "E92.5.1.2", {"start": v(134.56, 161.15) * mm, "end": v(148.5, 161.15) * mm});
            skLineSegment(sketch, "E92.5.1.3", {"start": v(134.56, 173.16) * mm, "end": v(134.56, 161.15) * mm});
            skLineSegment(sketch, "E92.5.2.0", {"start": v(134.56, 159.86) * mm, "end": v(148.5, 159.86) * mm});
            skLineSegment(sketch, "E92.5.2.1", {"start": v(148.5, 159.86) * mm, "end": v(148.5, 147.85) * mm});
            skLineSegment(sketch, "E92.5.2.2", {"start": v(134.56, 147.85) * mm, "end": v(148.5, 147.85) * mm});
            skLineSegment(sketch, "E92.5.2.3", {"start": v(134.56, 159.86) * mm, "end": v(134.56, 147.85) * mm});
            skLineSegment(sketch, "E92.6.0.0", {"start": v(149.76, 186.42) * mm, "end": v(163.7, 186.42) * mm});
            skLineSegment(sketch, "E92.6.0.1", {"start": v(163.7, 186.42) * mm, "end": v(163.7, 174.4) * mm});
            skLineSegment(sketch, "E92.6.0.2", {"start": v(149.76, 174.4) * mm, "end": v(163.7, 174.4) * mm});
            skLineSegment(sketch, "E92.6.0.3", {"start": v(149.76, 186.42) * mm, "end": v(149.76, 174.4) * mm});
            skLineSegment(sketch, "E92.6.1.0", {"start": v(149.76, 173.12) * mm, "end": v(163.7, 173.12) * mm});
            skLineSegment(sketch, "E92.6.1.1", {"start": v(163.7, 173.12) * mm, "end": v(163.7, 161.1) * mm});
            skLineSegment(sketch, "E92.6.1.2", {"start": v(149.76, 161.1) * mm, "end": v(163.7, 161.1) * mm});
            skLineSegment(sketch, "E92.6.1.3", {"start": v(149.76, 173.12) * mm, "end": v(149.76, 161.1) * mm});
            skLineSegment(sketch, "E92.6.2.0", {"start": v(149.76, 159.82) * mm, "end": v(163.7, 159.82) * mm});
            skLineSegment(sketch, "E92.6.2.1", {"start": v(163.7, 159.82) * mm, "end": v(163.7, 147.8) * mm});
            skLineSegment(sketch, "E92.6.2.2", {"start": v(149.76, 147.8) * mm, "end": v(163.7, 147.8) * mm});
            skLineSegment(sketch, "E92.6.2.3", {"start": v(149.76, 159.82) * mm, "end": v(149.76, 147.8) * mm});
            skLineSegment(sketch, "E92.direction1", {"start": v(58.56, 186.64) * mm, "end": v(73.76, 186.6) * mm, "construction": true});
            skLineSegment(sketch, "E92.direction2", {"start": v(58.56, 186.64) * mm, "end": v(58.56, 173.34) * mm, "construction": true});
            skSolve(sketch);
        }
        {
            var Q0;
            Q0=qCreatedBy(makeId("Top.planeOp"),FACE);
            var sketch = newSketch(context, id + "F2", { "sketchPlane" : qUnion([Q0])});
            skPoint(sketch, "E93.0", {"position": v(167.56, -50.86) * mm});
            skPoint(sketch, "E94.0", {"position": v(-71.69, 193.64) * mm});
            skLineSegment(sketch, "E95.bottom", {"start": v(167.56, -50.86) * mm, "end": v(-71.69, -50.86) * mm});
            skLineSegment(sketch, "E95.top", {"start": v(167.56, 193.64) * mm, "end": v(-71.69, 193.64) * mm});
            skLineSegment(sketch, "E95.left", {"start": v(167.56, -50.86) * mm, "end": v(167.56, 193.64) * mm});
            skLineSegment(sketch, "E95.right", {"start": v(-71.69, -50.86) * mm, "end": v(-71.69, 193.64) * mm});
            skSolve(sketch);
        }
        {
            var Q0;
            Q0=makeQuery(id+"F2.imprint","IMPRINT",FACE,{"disambiguationData":[TD([[makeQuery(id+"F2.imprint","IMPRINT",EDGE,{"derivedFrom":sQuery(id+"F2.wireOp",EDGE,"E95.bottom")}),-1.0]])]});
            extrude(context, id + "F3", {"entities" : qUnion([Q0]), "depth" : 1.5 * mm});
        }
        {
            var Q0;
            {var subQ3=sQuery(id+"F0.wireOp",EDGE,"E59.bottom");Q0=makeQuery(id+"F0.imprint","IMPRINT",FACE,{"disambiguationData":[TD([[makeQuery(id+"F0.imprint","IMPRINT",EDGE,{"derivedFrom":subQ3}),-1.0]])]});}
            var Q1;
            Q1=makeQuery(id+"F0.imprint","IMPRINT",FACE,{"disambiguationData":[TD([[makeQuery(id+"F0.imprint","IMPRINT",EDGE,{"derivedFrom":sQuery(id+"F0.wireOp",EDGE,"E60.bottom")}),1.0]])]});
            var Q2;
            Q2=makeQuery(id+"F0.imprint","IMPRINT",FACE,{"disambiguationData":[TD([[makeQuery(id+"F0.imprint","IMPRINT",EDGE,{"derivedFrom":sQuery(id+"F0.wireOp",EDGE,"E68.top")}),1.0]])]});
            var Q3;
            Q3=makeQuery(id+"F0.imprint","IMPRINT",FACE,{"disambiguationData":[TD([[makeQuery(id+"F0.imprint","IMPRINT",EDGE,{"derivedFrom":sQuery(id+"F0.wireOp",EDGE,"E67.bottom")}),1.0]])]});
            var Q4;
            Q4=makeQuery(id+"F0.imprint","IMPRINT",FACE,{"disambiguationData":[TD([[makeQuery(id+"F0.imprint","IMPRINT",EDGE,{"derivedFrom":sQuery(id+"F0.wireOp",EDGE,"E66.bottom")}),1.0]])]});
            var Q5;
            Q5=makeQuery(id+"F0.imprint","IMPRINT",FACE,{"disambiguationData":[TD([[makeQuery(id+"F0.imprint","IMPRINT",EDGE,{"derivedFrom":sQuery(id+"F0.wireOp",EDGE,"E58.top")}),1.0]])]});
            var Q6;
            {var subQ5=sQuery(id+"F0.wireOp",EDGE,"E57.bottom");Q6=makeQuery(id+"F0.imprint","IMPRINT",FACE,{"disambiguationData":[TD([[makeQuery(id+"F0.imprint","IMPRINT",EDGE,{"derivedFrom":subQ5}),1.0]])]});}
            var Q7;
            Q7=makeQuery(id+"F0.imprint","IMPRINT",FACE,{"disambiguationData":[TD([[makeQuery(id+"F0.imprint","IMPRINT",EDGE,{"derivedFrom":sQuery(id+"F0.wireOp",EDGE,"E63.bottom")}),-1.0]])]});
            var Q8;
            Q8=makeQuery(id+"F0.imprint","IMPRINT",FACE,{"disambiguationData":[TD([[makeQuery(id+"F0.imprint","IMPRINT",EDGE,{"derivedFrom":sQuery(id+"F0.wireOp",EDGE,"E62.bottom")}),-1.0]])]});
            var Q9;
            Q9=makeQuery(id+"F0.imprint","IMPRINT",FACE,{"disambiguationData":[TD([[makeQuery(id+"F0.imprint","IMPRINT",EDGE,{"derivedFrom":sQuery(id+"F0.wireOp",EDGE,"E64.top")}),-1.0]])]});
            var Q10;
            Q10=makeQuery(id+"F0.imprint","IMPRINT",FACE,{"disambiguationData":[TD([[makeQuery(id+"F0.imprint","IMPRINT",EDGE,{"derivedFrom":sQuery(id+"F0.wireOp",EDGE,"E13.bottom")}),-1.0]])]});
            var Q11;
            Q11=makeQuery(id+"F0.imprint","IMPRINT",FACE,{"disambiguationData":[TD([[makeQuery(id+"F0.imprint","IMPRINT",EDGE,{"derivedFrom":sQuery(id+"F0.wireOp",EDGE,"E8.bottom")}),-1.0]])]});
            var Q12;
            Q12=makeQuery(id+"F0.imprint","IMPRINT",FACE,{"disambiguationData":[TD([[makeQuery(id+"F0.imprint","IMPRINT",EDGE,{"derivedFrom":sQuery(id+"F0.wireOp",EDGE,"E9.bottom")}),1.0]])]});
            var Q13;
            Q13=makeQuery(id+"F0.imprint","IMPRINT",FACE,{"disambiguationData":[TD([[makeQuery(id+"F0.imprint","IMPRINT",EDGE,{"derivedFrom":sQuery(id+"F0.wireOp",EDGE,"E10.bottom")}),1.0]])]});
            var Q14;
            Q14=makeQuery(id+"F0.imprint","IMPRINT",FACE,{"disambiguationData":[TD([[makeQuery(id+"F0.imprint","IMPRINT",EDGE,{"derivedFrom":sQuery(id+"F0.wireOp",EDGE,"E0.top")}),-1.0]])]});
            var Q15;
            Q15=makeQuery(id+"F0.imprint","IMPRINT",FACE,{"disambiguationData":[TD([[makeQuery(id+"F0.imprint","IMPRINT",EDGE,{"derivedFrom":sQuery(id+"F0.wireOp",EDGE,"E55.bottom")}),-1.0]])]});
            var Q16;
            {var subQ2=sQuery(id+"F0.wireOp",EDGE,"E47.left");Q16=makeQuery(id+"F0.imprint","IMPRINT",FACE,{"disambiguationData":[TD([[makeQuery(id+"F0.imprint","IMPRINT",EDGE,{"derivedFrom":subQ2}),-1.0]])]});}
            var Q17;
            Q17=makeQuery(id+"F0.imprint","IMPRINT",FACE,{"disambiguationData":[TD([[makeQuery(id+"F0.imprint","IMPRINT",EDGE,{"derivedFrom":sQuery(id+"F0.wireOp",EDGE,"E56.bottom")}),-1.0]])]});
            var Q18;
            Q18=makeQuery(id+"F0.imprint","IMPRINT",FACE,{"disambiguationData":[TD([[makeQuery(id+"F0.imprint","IMPRINT",EDGE,{"derivedFrom":sQuery(id+"F0.wireOp",EDGE,"E53.top")}),-1.0]])]});
            var Q19;
            Q19=makeQuery(id+"F0.imprint","IMPRINT",FACE,{"disambiguationData":[TD([[makeQuery(id+"F0.imprint","IMPRINT",EDGE,{"derivedFrom":sQuery(id+"F0.wireOp",EDGE,"E51.bottom")}),-1.0]])]});
            var Q20;
            {var subQ5=sQuery(id+"F0.wireOp",EDGE,"E46.bottom");Q20=makeQuery(id+"F0.imprint","IMPRINT",FACE,{"disambiguationData":[TD([[makeQuery(id+"F0.imprint","IMPRINT",EDGE,{"derivedFrom":subQ5}),1.0]])]});}
            var Q21;
            Q21=makeQuery(id+"F0.imprint","IMPRINT",FACE,{"disambiguationData":[TD([[makeQuery(id+"F0.imprint","IMPRINT",EDGE,{"derivedFrom":sQuery(id+"F0.wireOp",EDGE,"E73.bottom")}),-1.0]])]});
            var Q22;
            Q22=makeQuery(id+"F0.imprint","IMPRINT",FACE,{"disambiguationData":[TD([[makeQuery(id+"F0.imprint","IMPRINT",EDGE,{"derivedFrom":sQuery(id+"F0.wireOp",EDGE,"E75.bottom")}),-1.0]])]});
            var Q23;
            {var subQ1=sQuery(id+"F0.wireOp",EDGE,"E49.left");Q23=makeQuery(id+"F0.imprint","IMPRINT",FACE,{"disambiguationData":[TD([[makeQuery(id+"F0.imprint","IMPRINT",EDGE,{"derivedFrom":subQ1}),1.0]])]});}
            var Q24;
            {var subQ1=sQuery(id+"F0.wireOp",EDGE,"E44.top");Q24=makeQuery(id+"F0.imprint","IMPRINT",FACE,{"disambiguationData":[TD([[makeQuery(id+"F0.imprint","IMPRINT",EDGE,{"derivedFrom":subQ1}),1.0]])]});}
            var Q25;
            {var subQ2=sQuery(id+"F0.wireOp",EDGE,"E43.bottom");Q25=makeQuery(id+"F0.imprint","IMPRINT",FACE,{"disambiguationData":[TD([[makeQuery(id+"F0.imprint","IMPRINT",EDGE,{"derivedFrom":subQ2}),1.0]])]});}
            var Q26;
            {var subQ0=sQuery(id+"F0.wireOp",EDGE,"E42.left");Q26=makeQuery(id+"F0.imprint","IMPRINT",FACE,{"disambiguationData":[TD([[makeQuery(id+"F0.imprint","IMPRINT",EDGE,{"derivedFrom":subQ0}),-1.0]])]});}
            var Q27;
            {var subQ3=sQuery(id+"F0.wireOp",EDGE,"E36.bottom");Q27=makeQuery(id+"F0.imprint","IMPRINT",FACE,{"disambiguationData":[TD([[makeQuery(id+"F0.imprint","IMPRINT",EDGE,{"derivedFrom":subQ3}),-1.0]])]});}
            var Q28;
            {var subQ1=sQuery(id+"F0.wireOp",EDGE,"E78.bottom");Q28=makeQuery(id+"F0.imprint","IMPRINT",FACE,{"disambiguationData":[TD([[makeQuery(id+"F0.imprint","IMPRINT",EDGE,{"derivedFrom":subQ1}),1.0]])]});}
            var Q29;
            {var subQ0=sQuery(id+"F0.wireOp",EDGE,"E38.bottom");Q29=makeQuery(id+"F0.imprint","IMPRINT",FACE,{"disambiguationData":[TD([[makeQuery(id+"F0.imprint","IMPRINT",EDGE,{"derivedFrom":subQ0}),-1.0]])]});}
            var Q30;
            {var subQ3=sQuery(id+"F0.wireOp",EDGE,"E21.bottom");Q30=makeQuery(id+"F0.imprint","IMPRINT",FACE,{"disambiguationData":[TD([[makeQuery(id+"F0.imprint","IMPRINT",EDGE,{"derivedFrom":subQ3}),1.0]])]});}
            var Q31;
            Q31=makeQuery(id+"F0.imprint","IMPRINT",FACE,{"disambiguationData":[TD([[makeQuery(id+"F0.imprint","IMPRINT",EDGE,{"derivedFrom":sQuery(id+"F0.wireOp",EDGE,"E24.bottom")}),-1.0]])]});
            var Q32;
            Q32=makeQuery(id+"F0.imprint","IMPRINT",FACE,{"disambiguationData":[TD([[makeQuery(id+"F0.imprint","IMPRINT",EDGE,{"derivedFrom":sQuery(id+"F0.wireOp",EDGE,"E19.bottom")}),-1.0]])]});
            var Q33;
            Q33=makeQuery(id+"F0.imprint","IMPRINT",FACE,{"disambiguationData":[TD([[makeQuery(id+"F0.imprint","IMPRINT",EDGE,{"derivedFrom":sQuery(id+"F0.wireOp",EDGE,"E20.bottom")}),-1.0]])]});
            var Q34;
            Q34=makeQuery(id+"F0.imprint","IMPRINT",FACE,{"disambiguationData":[TD([[makeQuery(id+"F0.imprint","IMPRINT",EDGE,{"derivedFrom":sQuery(id+"F0.wireOp",EDGE,"E18.bottom")}),1.0]])]});
            var Q35;
            Q35=makeQuery(id+"F0.imprint","IMPRINT",FACE,{"disambiguationData":[TD([[makeQuery(id+"F0.imprint","IMPRINT",EDGE,{"derivedFrom":sQuery(id+"F0.wireOp",EDGE,"E16.bottom")}),-1.0]])]});
            var Q36;
            Q36=makeQuery(id+"F0.imprint","IMPRINT",FACE,{"disambiguationData":[TD([[makeQuery(id+"F0.imprint","IMPRINT",EDGE,{"derivedFrom":sQuery(id+"F0.wireOp",EDGE,"E7.bottom")}),-1.0]])]});
            var Q37;
            Q37=makeQuery(id+"F0.imprint","IMPRINT",FACE,{"disambiguationData":[TD([[makeQuery(id+"F0.imprint","IMPRINT",EDGE,{"derivedFrom":sQuery(id+"F0.wireOp",EDGE,"E12.bottom")}),1.0]])]});
            var Q38;
            {var subQ1=sQuery(id+"F0.wireOp",EDGE,"E2.top");Q38=makeQuery(id+"F0.imprint","IMPRINT",FACE,{"disambiguationData":[TD([[makeQuery(id+"F0.imprint","IMPRINT",EDGE,{"derivedFrom":subQ1}),1.0]])]});}
            var Q39;
            {var subQ0=sQuery(id+"F0.wireOp",EDGE,"E1.bottom");Q39=makeQuery(id+"F0.imprint","IMPRINT",FACE,{"disambiguationData":[TD([[makeQuery(id+"F0.imprint","IMPRINT",EDGE,{"derivedFrom":subQ0}),1.0]])]});}
            var Q40;
            {var subQ0=sQuery(id+"F0.wireOp",EDGE,"E4.bottom");Q40=makeQuery(id+"F0.imprint","IMPRINT",FACE,{"disambiguationData":[TD([[makeQuery(id+"F0.imprint","IMPRINT",EDGE,{"derivedFrom":subQ0}),1.0]])]});}
            var Q41;
            {var subQ3=sQuery(id+"F0.wireOp",EDGE,"E5.top");Q41=makeQuery(id+"F0.imprint","IMPRINT",FACE,{"disambiguationData":[TD([[makeQuery(id+"F0.imprint","IMPRINT",EDGE,{"derivedFrom":subQ3}),1.0]])]});}
            var Q42;
            {var subQ0=sQuery(id+"F0.wireOp",EDGE,"E15.bottom");Q42=makeQuery(id+"F0.imprint","IMPRINT",FACE,{"disambiguationData":[TD([[makeQuery(id+"F0.imprint","IMPRINT",EDGE,{"derivedFrom":subQ0}),-1.0]])]});}
            var Q43;
            {var subQ4=sQuery(id+"F0.wireOp",EDGE,"E23.bottom");Q43=makeQuery(id+"F0.imprint","IMPRINT",FACE,{"disambiguationData":[TD([[makeQuery(id+"F0.imprint","IMPRINT",EDGE,{"derivedFrom":subQ4}),-1.0]])]});}
            var Q44;
            Q44=makeQuery(id+"F0.imprint","IMPRINT",FACE,{"disambiguationData":[TD([[makeQuery(id+"F0.imprint","IMPRINT",EDGE,{"derivedFrom":sQuery(id+"F0.wireOp",EDGE,"E26.bottom")}),1.0]])]});
            var Q45;
            {var subQ0=sQuery(id+"F0.wireOp",EDGE,"E28.bottom");Q45=makeQuery(id+"F0.imprint","IMPRINT",FACE,{"disambiguationData":[TD([[makeQuery(id+"F0.imprint","IMPRINT",EDGE,{"derivedFrom":subQ0}),1.0]])]});}
            var Q46;
            {var subQ5=sQuery(id+"F0.wireOp",EDGE,"E29.left");Q46=makeQuery(id+"F0.imprint","IMPRINT",FACE,{"disambiguationData":[TD([[makeQuery(id+"F0.imprint","IMPRINT",EDGE,{"derivedFrom":subQ5}),-1.0]])]});}
            var Q47;
            {var subQ5=sQuery(id+"F0.wireOp",EDGE,"E29.right");Q47=makeQuery(id+"F0.imprint","IMPRINT",FACE,{"disambiguationData":[TD([[makeQuery(id+"F0.imprint","IMPRINT",EDGE,{"derivedFrom":subQ5}),1.0]])]});}
            var Q48;
            Q48=makeQuery(id+"F0.imprint","IMPRINT",FACE,{"disambiguationData":[TD([[makeQuery(id+"F0.imprint","IMPRINT",EDGE,{"derivedFrom":sQuery(id+"F0.wireOp",EDGE,"E33.top")}),1.0]])]});
            var Q49;
            Q49=makeQuery(id+"F0.imprint","IMPRINT",FACE,{"disambiguationData":[TD([[makeQuery(id+"F0.imprint","IMPRINT",EDGE,{"derivedFrom":sQuery(id+"F0.wireOp",EDGE,"E34.bottom")}),-1.0]])]});
            var Q50;
            Q50=makeQuery(id+"F0.imprint","IMPRINT",FACE,{"disambiguationData":[TD([[makeQuery(id+"F0.imprint","IMPRINT",EDGE,{"derivedFrom":sQuery(id+"F0.wireOp",EDGE,"E31.bottom")}),-1.0]])]});
            var Q51;
            {var subQ1=sQuery(id+"F0.wireOp",EDGE,"E40.bottom");Q51=makeQuery(id+"F0.imprint","IMPRINT",FACE,{"disambiguationData":[TD([[makeQuery(id+"F0.imprint","IMPRINT",EDGE,{"derivedFrom":subQ1}),-1.0]])]});}
            var Q52;
            Q52=makeQuery(id+"F0.imprint","IMPRINT",FACE,{"disambiguationData":[TD([[makeQuery(id+"F0.imprint","IMPRINT",EDGE,{"derivedFrom":sQuery(id+"F0.wireOp",EDGE,"E71.bottom")}),-1.0]])]});
            var Q53;
            {var subQ3=sQuery(id+"F0.wireOp",EDGE,"E81.bottom");Q53=makeQuery(id+"F0.imprint","IMPRINT",FACE,{"disambiguationData":[TD([[makeQuery(id+"F0.imprint","IMPRINT",EDGE,{"derivedFrom":subQ3}),1.0]])]});}
            var Q54;
            Q54=makeQuery(id+"F0.imprint","IMPRINT",FACE,{"disambiguationData":[TD([[makeQuery(id+"F0.imprint","IMPRINT",EDGE,{"derivedFrom":sQuery(id+"F0.wireOp",EDGE,"E83.bottom")}),-1.0]])]});
            var Q55;
            Q55=makeQuery(id+"F0.imprint","IMPRINT",FACE,{"disambiguationData":[TD([[makeQuery(id+"F0.imprint","IMPRINT",EDGE,{"derivedFrom":sQuery(id+"F0.wireOp",EDGE,"E80.bottom")}),-1.0]])]});
            var Q56;
            Q56=makeQuery(id+"F0.imprint","IMPRINT",FACE,{"disambiguationData":[TD([[makeQuery(id+"F0.imprint","IMPRINT",EDGE,{"derivedFrom":sQuery(id+"F0.wireOp",EDGE,"E82.bottom")}),1.0]])]});
            extrude(context, id + "F4", {"entities" : qUnion([Q0, Q1, Q2, Q3, Q4, Q5, Q6, Q7, Q8, Q9, Q10, Q11, Q12, Q13, Q14, Q15, Q16, Q17, Q18, Q19, Q20, Q21, Q22, Q23, Q24, Q25, Q26, Q27, Q28, Q29, Q30, Q31, Q32, Q33, Q34, Q35, Q36, Q37, Q38, Q39, Q40, Q41, Q42, Q43, Q44, Q45, Q46, Q47, Q48, Q49, Q50, Q51, Q52, Q53, Q54, Q55, Q56]), "operationType" : NewBodyOperationType.ADD, "depth" : 17 * mm});
        }
        {
            var Q0;
            Q0=makeQuery(id+"F0.imprint","IMPRINT",FACE,{"disambiguationData":[TD([[makeQuery(id+"F0.imprint","IMPRINT",EDGE,{"derivedFrom":sQuery(id+"F0.wireOp",EDGE,"E76.bottom")}),1.0]])]});
            var Q1;
            Q1=makeQuery(id+"F0.imprint","IMPRINT",FACE,{"disambiguationData":[TD([[makeQuery(id+"F0.imprint","IMPRINT",EDGE,{"derivedFrom":sQuery(id+"F0.wireOp",EDGE,"E79.bottom")}),-1.0]])]});
            var Q2;
            Q2=makeQuery(id+"F0.imprint","IMPRINT",FACE,{"disambiguationData":[TD([[makeQuery(id+"F0.imprint","IMPRINT",EDGE,{"derivedFrom":sQuery(id+"F0.wireOp",EDGE,"E67.top")}),1.0]])]});
            var Q3;
            Q3=makeQuery(id+"F0.imprint","IMPRINT",FACE,{"disambiguationData":[TD([[makeQuery(id+"F0.imprint","IMPRINT",EDGE,{"derivedFrom":sQuery(id+"F0.wireOp",EDGE,"E61.bottom")}),1.0]])]});
            var Q4;
            Q4=makeQuery(id+"F0.imprint","IMPRINT",FACE,{"disambiguationData":[TD([[makeQuery(id+"F0.imprint","IMPRINT",EDGE,{"derivedFrom":sQuery(id+"F0.wireOp",EDGE,"E16.top")}),-1.0]])]});
            var Q5;
            Q5=makeQuery(id+"F0.imprint","IMPRINT",FACE,{"disambiguationData":[TD([[makeQuery(id+"F0.imprint","IMPRINT",EDGE,{"derivedFrom":sQuery(id+"F0.wireOp",EDGE,"E65.bottom")}),-1.0]])]});
            var Q6;
            Q6=makeQuery(id+"F0.imprint","IMPRINT",FACE,{"disambiguationData":[TD([[makeQuery(id+"F0.imprint","IMPRINT",EDGE,{"derivedFrom":sQuery(id+"F0.wireOp",EDGE,"E49.bottom")}),1.0]])]});
            var Q7;
            Q7=makeQuery(id+"F0.imprint","IMPRINT",FACE,{"disambiguationData":[TD([[makeQuery(id+"F0.imprint","IMPRINT",EDGE,{"derivedFrom":sQuery(id+"F0.wireOp",EDGE,"E32.bottom")}),1.0]])]});
            var Q8;
            Q8=makeQuery(id+"F0.imprint","IMPRINT",FACE,{"disambiguationData":[TD([[makeQuery(id+"F0.imprint","IMPRINT",EDGE,{"derivedFrom":sQuery(id+"F0.wireOp",EDGE,"E84.bottom")}),-1.0]])]});
            extrude(context, id + "F5", {"entities" : qUnion([Q0, Q1, Q2, Q3, Q4, Q5, Q6, Q7, Q8]), "operationType" : NewBodyOperationType.ADD, "depth" : (1.5 + 0.6) * mm});
        }
        {
            var Q0;
            {var subQ4=sQuery(id+"F0.wireOp",EDGE,"E33.right");Q0=makeQuery(id+"F0.imprint","IMPRINT",FACE,{"disambiguationData":[TD([[makeQuery(id+"F0.imprint","IMPRINT",EDGE,{"derivedFrom":subQ4}),1.0]])]});}
            var Q1;
            {var subQ0=sQuery(id+"F0.wireOp",EDGE,"E6.top");Q1=makeQuery(id+"F0.imprint","IMPRINT",FACE,{"disambiguationData":[TD([[makeQuery(id+"F0.imprint","IMPRINT",EDGE,{"derivedFrom":subQ0}),1.0]])]});}
            var Q2;
            {var subQ0=sQuery(id+"F0.wireOp",EDGE,"E4.top");Q2=makeQuery(id+"F0.imprint","IMPRINT",FACE,{"disambiguationData":[TD([[makeQuery(id+"F0.imprint","IMPRINT",EDGE,{"derivedFrom":subQ0}),1.0]])]});}
            var Q3;
            {var subQ0=sQuery(id+"F0.wireOp",EDGE,"E1.top");Q3=makeQuery(id+"F0.imprint","IMPRINT",FACE,{"disambiguationData":[TD([[makeQuery(id+"F0.imprint","IMPRINT",EDGE,{"derivedFrom":subQ0}),1.0]])]});}
            var Q4;
            {var subQ0=sQuery(id+"F0.wireOp",EDGE,"E43.top");Q4=makeQuery(id+"F0.imprint","IMPRINT",FACE,{"disambiguationData":[TD([[makeQuery(id+"F0.imprint","IMPRINT",EDGE,{"derivedFrom":subQ0}),1.0]])]});}
            extrude(context, id + "F6", {"entities" : qUnion([Q0, Q1, Q2, Q3, Q4]), "operationType" : NewBodyOperationType.ADD, "depth" : 4 * mm});
        }
        {
            var Q0;
            Q0=makeQuery(id+"F1.imprint","IMPRINT",FACE,{"disambiguationData":[TD([[makeQuery(id+"F1.imprint","IMPRINT",EDGE,{"derivedFrom":sQuery(id+"F1.wireOp",EDGE,"E92.1.0.0")}),-1.0]])]});
            var Q1;
            Q1=makeQuery(id+"F1.imprint","IMPRINT",FACE,{"disambiguationData":[TD([[makeQuery(id+"F1.imprint","IMPRINT",EDGE,{"derivedFrom":sQuery(id+"F1.wireOp",EDGE,"E91.bottom")}),-1.0]])]});
            var Q2;
            Q2=makeQuery(id+"F1.imprint","IMPRINT",FACE,{"disambiguationData":[TD([[makeQuery(id+"F1.imprint","IMPRINT",EDGE,{"derivedFrom":sQuery(id+"F1.wireOp",EDGE,"E92.2.0.0")}),-1.0]])]});
            var Q3;
            Q3=makeQuery(id+"F1.imprint","IMPRINT",FACE,{"disambiguationData":[TD([[makeQuery(id+"F1.imprint","IMPRINT",EDGE,{"derivedFrom":sQuery(id+"F1.wireOp",EDGE,"E92.3.0.0")}),-1.0]])]});
            var Q4;
            Q4=makeQuery(id+"F1.imprint","IMPRINT",FACE,{"disambiguationData":[TD([[makeQuery(id+"F1.imprint","IMPRINT",EDGE,{"derivedFrom":sQuery(id+"F1.wireOp",EDGE,"E92.4.0.0")}),-1.0]])]});
            var Q5;
            Q5=makeQuery(id+"F1.imprint","IMPRINT",FACE,{"disambiguationData":[TD([[makeQuery(id+"F1.imprint","IMPRINT",EDGE,{"derivedFrom":sQuery(id+"F1.wireOp",EDGE,"E92.5.0.0")}),-1.0]])]});
            var Q6;
            {var subQ0=sQuery(id+"F1.wireOp",EDGE,"E92.6.0.3");Q6=makeQuery(id+"F1.imprint","IMPRINT",FACE,{"disambiguationData":[TD([[makeQuery(id+"F1.imprint","IMPRINT",EDGE,{"derivedFrom":subQ0}),1.0]])]});}
            var Q7;
            {var subQ5=sQuery(id+"F1.wireOp",EDGE,"E92.6.1.3");Q7=makeQuery(id+"F1.imprint","IMPRINT",FACE,{"disambiguationData":[TD([[makeQuery(id+"F1.imprint","IMPRINT",EDGE,{"derivedFrom":subQ5}),1.0]])]});}
            var Q8;
            Q8=makeQuery(id+"F1.imprint","IMPRINT",FACE,{"disambiguationData":[TD([[makeQuery(id+"F1.imprint","IMPRINT",EDGE,{"derivedFrom":sQuery(id+"F1.wireOp",EDGE,"E92.5.1.0")}),-1.0]])]});
            var Q9;
            Q9=makeQuery(id+"F1.imprint","IMPRINT",FACE,{"disambiguationData":[TD([[makeQuery(id+"F1.imprint","IMPRINT",EDGE,{"derivedFrom":sQuery(id+"F1.wireOp",EDGE,"E92.4.1.0")}),-1.0]])]});
            var Q10;
            Q10=makeQuery(id+"F1.imprint","IMPRINT",FACE,{"disambiguationData":[TD([[makeQuery(id+"F1.imprint","IMPRINT",EDGE,{"derivedFrom":sQuery(id+"F1.wireOp",EDGE,"E92.3.1.0")}),-1.0]])]});
            var Q11;
            Q11=makeQuery(id+"F1.imprint","IMPRINT",FACE,{"disambiguationData":[TD([[makeQuery(id+"F1.imprint","IMPRINT",EDGE,{"derivedFrom":sQuery(id+"F1.wireOp",EDGE,"E92.2.1.0")}),-1.0]])]});
            var Q12;
            Q12=makeQuery(id+"F1.imprint","IMPRINT",FACE,{"disambiguationData":[TD([[makeQuery(id+"F1.imprint","IMPRINT",EDGE,{"derivedFrom":sQuery(id+"F1.wireOp",EDGE,"E92.1.1.0")}),-1.0]])]});
            var Q13;
            Q13=makeQuery(id+"F1.imprint","IMPRINT",FACE,{"disambiguationData":[TD([[makeQuery(id+"F1.imprint","IMPRINT",EDGE,{"derivedFrom":sQuery(id+"F1.wireOp",EDGE,"E92.0.1.0")}),-1.0]])]});
            var Q14;
            Q14=makeQuery(id+"F1.imprint","IMPRINT",FACE,{"disambiguationData":[TD([[makeQuery(id+"F1.imprint","IMPRINT",EDGE,{"derivedFrom":sQuery(id+"F1.wireOp",EDGE,"E92.0.2.0")}),-1.0]])]});
            var Q15;
            Q15=makeQuery(id+"F1.imprint","IMPRINT",FACE,{"disambiguationData":[TD([[makeQuery(id+"F1.imprint","IMPRINT",EDGE,{"derivedFrom":sQuery(id+"F1.wireOp",EDGE,"E92.1.2.0")}),-1.0]])]});
            var Q16;
            Q16=makeQuery(id+"F1.imprint","IMPRINT",FACE,{"disambiguationData":[TD([[makeQuery(id+"F1.imprint","IMPRINT",EDGE,{"derivedFrom":sQuery(id+"F1.wireOp",EDGE,"E92.2.2.0")}),-1.0]])]});
            var Q17;
            Q17=makeQuery(id+"F1.imprint","IMPRINT",FACE,{"disambiguationData":[TD([[makeQuery(id+"F1.imprint","IMPRINT",EDGE,{"derivedFrom":sQuery(id+"F1.wireOp",EDGE,"E92.3.2.0")}),-1.0]])]});
            var Q18;
            Q18=makeQuery(id+"F1.imprint","IMPRINT",FACE,{"disambiguationData":[TD([[makeQuery(id+"F1.imprint","IMPRINT",EDGE,{"derivedFrom":sQuery(id+"F1.wireOp",EDGE,"E92.4.2.0")}),-1.0]])]});
            var Q19;
            Q19=makeQuery(id+"F1.imprint","IMPRINT",FACE,{"disambiguationData":[TD([[makeQuery(id+"F1.imprint","IMPRINT",EDGE,{"derivedFrom":sQuery(id+"F1.wireOp",EDGE,"E92.5.2.0")}),-1.0]])]});
            var Q20;
            {var subQ0=sQuery(id+"F1.wireOp",EDGE,"E92.6.2.3");Q20=makeQuery(id+"F1.imprint","IMPRINT",FACE,{"disambiguationData":[TD([[makeQuery(id+"F1.imprint","IMPRINT",EDGE,{"derivedFrom":subQ0}),1.0]])]});}
            extrude(context, id + "F7", {"entities" : qUnion([Q0, Q1, Q2, Q3, Q4, Q5, Q6, Q7, Q8, Q9, Q10, Q11, Q12, Q13, Q14, Q15, Q16, Q17, Q18, Q19, Q20]), "operationType" : NewBodyOperationType.ADD, "depth" : (1.5 + 0.3) * mm});
        }
    });
